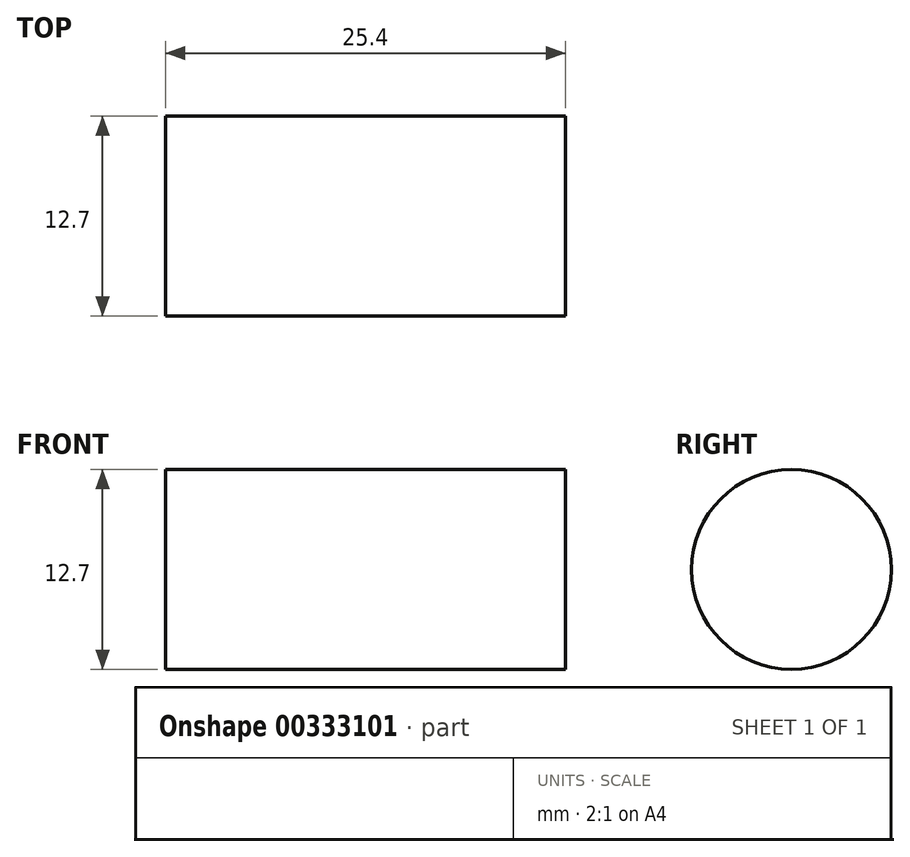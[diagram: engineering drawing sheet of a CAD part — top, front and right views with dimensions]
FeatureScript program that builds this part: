
annotation { "Feature Type Name" : "Feature", "Feature Type Description" : "" }
export const myFeature = defineFeature(function(context is Context, id is Id, definition is map)
    precondition{}
    {
        {
            var Q0;
            Q0=qCreatedBy(makeId("Right.planeOp"),FACE);
            var sketch = newSketch(context, id + "F0", { "sketchPlane" : qUnion([Q0])});
            skCircle(sketch, "E0", {"center": v(0, 0) * mm, "radius": 6.35 * mm});
            skSolve(sketch);
        }
        {
            var Q0;
            Q0=qSketchRegion(id+"F0",true);
            extrude(context, id + "F1", {"entities" : qUnion([Q0]), "depth" : 25.4 * mm});
        }
    });
